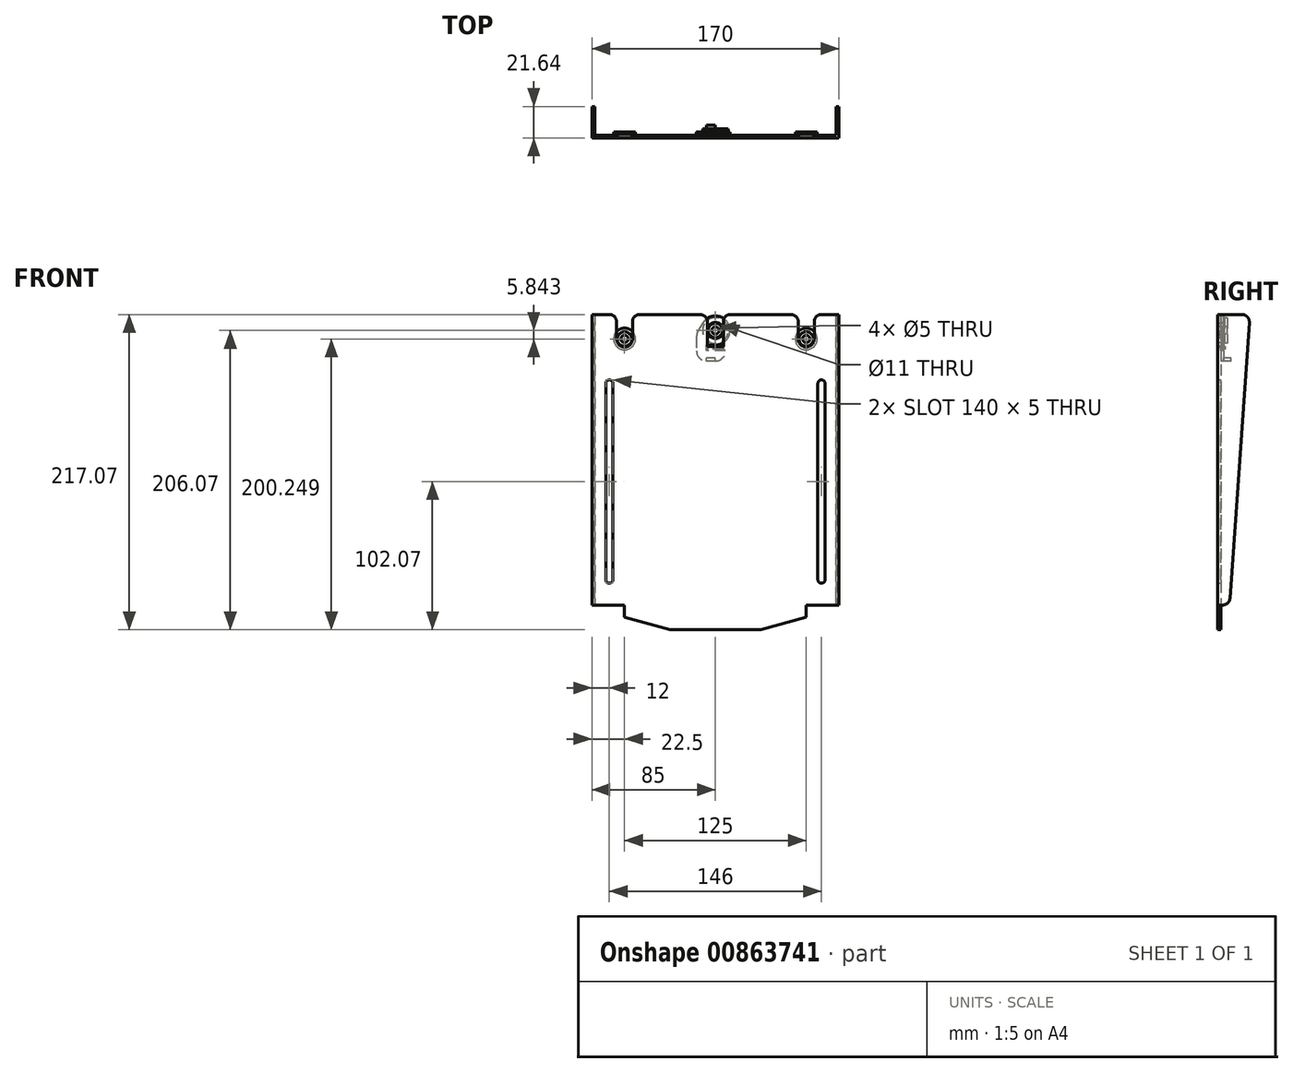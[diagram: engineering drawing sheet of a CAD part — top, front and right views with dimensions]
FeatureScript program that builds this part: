
annotation { "Feature Type Name" : "Feature", "Feature Type Description" : "" }
export const myFeature = defineFeature(function(context is Context, id is Id, definition is map)
    precondition{}
    {
        {
            var Q0;
            Q0=qCreatedBy(makeId("Front.planeOp"),FACE);
            var sketch = newSketch(context, id + "F0", { "sketchPlane" : qUnion([Q0])});
            skLineSegment(sketch, "E0.top", {"start": v(0, -100) * mm, "end": v(85, -100) * mm});
            skLineSegment(sketch, "E0.left", {"start": v(0, 100) * mm, "end": v(0, -100) * mm});
            skLineSegment(sketch, "E0.right", {"start": v(85, 100) * mm, "end": v(85, -100) * mm});
            skPoint(sketch, "E0.middle", {"position": v(42.5, 0) * mm});
            skLineSegment(sketch, "E1.left", {"start": v(0, 100) * mm, "end": v(0, 105) * mm});
            skLineSegment(sketch, "E2.MirrorCS", {"start": v(-85, 100) * mm, "end": v(-85, -100) * mm});
            skLineSegment(sketch, "E3.MirrorCS", {"start": v(0, -100) * mm, "end": v(-85, -100) * mm});
            skPoint(sketch, "E4.MirrorP", {"position": v(-42.5, 0) * mm});
            skLineSegment(sketch, "E5.bottom", {"start": v(73, -85) * mm, "end": v(73, -85) * mm});
            skLineSegment(sketch, "E5.top", {"start": v(73, 55) * mm, "end": v(73, 55) * mm});
            skLineSegment(sketch, "E5.left", {"start": v(70.5, -82.5) * mm, "end": v(70.5, 52.5) * mm});
            skLineSegment(sketch, "E5.right", {"start": v(75.5, -82.5) * mm, "end": v(75.5, 52.5) * mm});
            skPoint(sketch, "E5.middle", {"position": v(73, -15) * mm});
            skPoint(sketch, "E6.visualSharp", {"position": v(70.5, -85) * mm});
            skArc(sketch, "E6.filletArc", {"start": v(70.5, -82.5) * mm, "mid": v(71.23, -84.27) * mm, "end": v(73, -85) * mm});
            skPoint(sketch, "E7.visualSharp", {"position": v(75.5, -85) * mm});
            skArc(sketch, "E7.filletArc", {"start": v(73, -85) * mm, "mid": v(74.77, -84.27) * mm, "end": v(75.5, -82.5) * mm});
            skPoint(sketch, "E8.visualSharp", {"position": v(70.5, 55) * mm});
            skArc(sketch, "E8.filletArc", {"start": v(73, 55) * mm, "mid": v(71.23, 54.27) * mm, "end": v(70.5, 52.5) * mm});
            skPoint(sketch, "E9.visualSharp", {"position": v(75.5, 55) * mm});
            skArc(sketch, "E9.filletArc", {"start": v(75.5, 52.5) * mm, "mid": v(74.77, 54.27) * mm, "end": v(73, 55) * mm});
            skArc(sketch, "E10.MirrorCS", {"start": v(-70.5, -82.5) * mm, "mid": v(-71.23, -84.27) * mm, "end": v(-73, -85) * mm});
            skArc(sketch, "E11.MirrorCS", {"start": v(-75.5, 52.5) * mm, "mid": v(-74.77, 54.27) * mm, "end": v(-73, 55) * mm});
            skArc(sketch, "E12.MirrorCS", {"start": v(-73, -85) * mm, "mid": v(-74.77, -84.27) * mm, "end": v(-75.5, -82.5) * mm});
            skArc(sketch, "E13.MirrorCS", {"start": v(-73, 55) * mm, "mid": v(-71.23, 54.27) * mm, "end": v(-70.5, 52.5) * mm});
            skLineSegment(sketch, "E14.MirrorCS", {"start": v(-70.5, -82.5) * mm, "end": v(-70.5, 52.5) * mm});
            skLineSegment(sketch, "E15.MirrorCS", {"start": v(-75.5, -82.5) * mm, "end": v(-75.5, 52.5) * mm});
            skPoint(sketch, "E16.MirrorP", {"position": v(-70.5, -85) * mm});
            skPoint(sketch, "E17.MirrorP", {"position": v(-75.5, -85) * mm});
            skPoint(sketch, "E18.MirrorP", {"position": v(-75.5, 55) * mm});
            skPoint(sketch, "E19.MirrorP", {"position": v(-73, -15) * mm});
            skPoint(sketch, "E20.MirrorP", {"position": v(-70.5, 55) * mm});
            skLineSegment(sketch, "E21.MirrorCS", {"start": v(-73, -85) * mm, "end": v(-73, -85) * mm});
            skLineSegment(sketch, "E22.MirrorCS", {"start": v(-73, 55) * mm, "end": v(-73, 55) * mm});
            skLineSegment(sketch, "E23", {"start": v(0, -100) * mm, "end": v(0, -117.07) * mm});
            skLineSegment(sketch, "E24", {"start": v(0, -117.07) * mm, "end": v(-31.25, -117.07) * mm});
            skLineSegment(sketch, "E25", {"start": v(-62.5, -100) * mm, "end": v(-62.5, -108.5) * mm});
            skLineSegment(sketch, "E26", {"start": v(-62.5, -108.5) * mm, "end": v(-31.25, -117.07) * mm});
            skLineSegment(sketch, "E27.MirrorCS", {"start": v(62.5, -100) * mm, "end": v(62.5, -108.5) * mm});
            skLineSegment(sketch, "E28.MirrorCS", {"start": v(0, -117.07) * mm, "end": v(31.25, -117.07) * mm});
            skLineSegment(sketch, "E29.MirrorCS", {"start": v(62.5, -108.5) * mm, "end": v(31.25, -117.07) * mm});
            skLineSegment(sketch, "E30", {"start": v(-85, 100) * mm, "end": v(-73, 100) * mm});
            skLineSegment(sketch, "E31", {"start": v(-68, 95) * mm, "end": v(-68, 83.18) * mm});
            skLineSegment(sketch, "E32", {"start": v(-62.5, 77.68) * mm, "end": v(-62.5, 77.68) * mm});
            skLineSegment(sketch, "E33", {"start": v(-57, 83.18) * mm, "end": v(-57, 95) * mm});
            skPoint(sketch, "E34.visualSharp", {"position": v(-68, 77.68) * mm});
            skArc(sketch, "E34.filletArc", {"start": v(-68, 83.18) * mm, "mid": v(-66.39, 79.29) * mm, "end": v(-62.5, 77.68) * mm});
            skPoint(sketch, "E35.visualSharp", {"position": v(-57, 77.68) * mm});
            skArc(sketch, "E35.filletArc", {"start": v(-62.5, 77.68) * mm, "mid": v(-58.61, 79.29) * mm, "end": v(-57, 83.18) * mm});
            skLineSegment(sketch, "E36.MirrorCS", {"start": v(57, 83.18) * mm, "end": v(57, 95) * mm});
            skPoint(sketch, "E37.MirrorP", {"position": v(57, 77.68) * mm});
            skArc(sketch, "E38.MirrorCS", {"start": v(62.5, 77.68) * mm, "mid": v(58.61, 79.29) * mm, "end": v(57, 83.18) * mm});
            skArc(sketch, "E39.MirrorCS", {"start": v(68, 83.18) * mm, "mid": v(66.39, 79.29) * mm, "end": v(62.5, 77.68) * mm});
            skLineSegment(sketch, "E40.MirrorCS", {"start": v(68, 95) * mm, "end": v(68, 83.18) * mm});
            skLineSegment(sketch, "E41.MirrorCS", {"start": v(85, 100) * mm, "end": v(73, 100) * mm});
            skPoint(sketch, "E42.visualSharp", {"position": v(57, 100) * mm});
            skArc(sketch, "E42.filletArc", {"start": v(57, 95) * mm, "mid": v(55.54, 98.54) * mm, "end": v(52, 100) * mm});
            skPoint(sketch, "E43.visualSharp", {"position": v(68, 100) * mm});
            skArc(sketch, "E43.filletArc", {"start": v(73, 100) * mm, "mid": v(69.46, 98.54) * mm, "end": v(68, 95) * mm});
            skPoint(sketch, "E44.visualSharp", {"position": v(-57, 100) * mm});
            skArc(sketch, "E44.filletArc", {"start": v(-52, 100) * mm, "mid": v(-55.54, 98.54) * mm, "end": v(-57, 95) * mm});
            skPoint(sketch, "E45.visualSharp", {"position": v(-68, 100) * mm});
            skArc(sketch, "E45.filletArc", {"start": v(-68, 95) * mm, "mid": v(-69.46, 98.54) * mm, "end": v(-73, 100) * mm});
            skLineSegment(sketch, "E46", {"start": v(5.5, 95) * mm, "end": v(5.5, 78) * mm});
            skLineSegment(sketch, "E47", {"start": v(5.5, 78) * mm, "end": v(-5.5, 78) * mm});
            skLineSegment(sketch, "E48", {"start": v(-5.5, 78) * mm, "end": v(-5.5, 95) * mm});
            skLineSegment(sketch, "E49", {"start": v(52, 100) * mm, "end": v(10.5, 100) * mm});
            skLineSegment(sketch, "E50", {"start": v(-52, 100) * mm, "end": v(-10.5, 100) * mm});
            skPoint(sketch, "E51.visualSharp", {"position": v(-5.5, 100) * mm});
            skArc(sketch, "E51.filletArc", {"start": v(-5.5, 95) * mm, "mid": v(-6.96, 98.54) * mm, "end": v(-10.5, 100) * mm});
            skPoint(sketch, "E52.visualSharp", {"position": v(5.5, 100) * mm});
            skArc(sketch, "E52.filletArc", {"start": v(10.5, 100) * mm, "mid": v(6.96, 98.54) * mm, "end": v(5.5, 95) * mm});
            skSolve(sketch);
        }
        {
            var Q0;
            Q0=qSketchRegion(id+"F0",true);
            extrude(context, id + "F1", {"entities" : qUnion([Q0]), "depth" : 2 * mm, "offsetDistance" : 25 * mm});
        }
        {
            var Q0;
            Q0=makeQuery(id+"F1.opExtrude","CAP_FACE",FACE,{"disambiguationData":[OSD([sQuery(id+"F0.wireOp",EDGE,"E0.bottom"),sQuery(id+"F0.wireOp",EDGE,"E0.top"),sQuery(id+"F0.wireOp",EDGE,"E0.right"),sQuery(id+"F0.wireOp",EDGE,"frcyEhX3-ksV9-Io33-VOOh-hWverEK9uXBL.left"),sQuery(id+"F0.wireOp",EDGE,"frcyEhX3-ksV9-Io33-VOOh-hWverEK9uXBL.right"),sQuery(id+"F0.wireOp",EDGE,"ycnwuAfa-UpH9-AvOl-Gm3H-XGRiDgKgmbUQ"),sQuery(id+"F0.wireOp",EDGE,"YSR243FN-PfGp-wJLQ-lxfN-2wXKMQRAt0pg"),sQuery(id+"F0.wireOp",EDGE,"E1.bottom"),sQuery(id+"F0.wireOp",EDGE,"f4791902-98f6-4560-8930-070e0529dc460.MirrorCS"),sQuery(id+"F0.wireOp",EDGE,"f4791902-98f6-4560-8930-070e0529dc461.MirrorCS"),sQuery(id+"F0.wireOp",EDGE,"E2.MirrorCS"),sQuery(id+"F0.wireOp",EDGE,"f4791902-98f6-4560-8930-070e0529dc4612.MirrorCS"),sQuery(id+"F0.wireOp",EDGE,"f4791902-98f6-4560-8930-070e0529dc4615.MirrorCS"),sQuery(id+"F0.wireOp",EDGE,"E3.MirrorCS"),sQuery(id+"F0.wireOp",EDGE,"f4791902-98f6-4560-8930-070e0529dc4617.MirrorCS"),sQuery(id+"F0.wireOp",EDGE,"f4791902-98f6-4560-8930-070e0529dc4623.MirrorCS")])],"isStart":true});
            var sketch = newSketch(context, id + "F2", { "sketchPlane" : qUnion([Q0])});
            skArc(sketch, "E53", {"start": v(-10, 89) * mm, "mid": v(-7.07, 81.93) * mm, "end": v(0, 79) * mm});
            skCircle(sketch, "E54", {"center": v(0, 89) * mm, "radius": 5.5 * mm});
            skLineSegment(sketch, "E55", {"start": v(0, 79) * mm, "end": v(6, 79) * mm});
            skLineSegment(sketch, "E56", {"start": v(-7, 75) * mm, "end": v(6, 75) * mm});
            skLineSegment(sketch, "E57", {"start": v(6, 75) * mm, "end": v(6, 79) * mm});
            skArc(sketch, "E58", {"start": v(-7, 75) * mm, "mid": v(-4.95, 70.05) * mm, "end": v(0, 68) * mm});
            skLineSegment(sketch, "E59", {"start": v(13, 84.44) * mm, "end": v(13, 75) * mm});
            skLineSegment(sketch, "E60", {"start": v(0, 68) * mm, "end": v(6, 68) * mm});
            skPoint(sketch, "E61.visualSharp", {"position": v(13, 68) * mm});
            skArc(sketch, "E61.filletArc", {"start": v(6, 68) * mm, "mid": v(10.95, 70.05) * mm, "end": v(13, 75) * mm});
            skPoint(sketch, "E62.visualSharp", {"position": v(13, 89) * mm});
            skLineSegment(sketch, "E63", {"start": v(11.65, 89.18) * mm, "end": v(8.5, 94.26) * mm});
            skArc(sketch, "E64", {"start": v(0, 79) * mm, "mid": v(-8.74, 93.87) * mm, "end": v(8.5, 94.26) * mm});
            skPoint(sketch, "E65.visualSharp", {"position": v(13, 87) * mm});
            skArc(sketch, "E65.filletArc", {"start": v(13, 84.44) * mm, "mid": v(12.66, 86.9) * mm, "end": v(11.65, 89.18) * mm});
            skSolve(sketch);
        }
        {
            var Q0;
            Q0=qSketchRegion(id+"F2",true);
            extrude(context, id + "F3", {"entities" : qUnion([Q0]), "depth" : 2 * mm, "offsetDistance" : 25 * mm});
        }
        {
            var Q0;
            Q0=makeQuery(id+"F1.opExtrude","SWEPT_FACE",FACE,{"disambiguationData":[OSD([sQuery(id+"F0.wireOp",EDGE,"E2.MirrorCS")])]});
            var sketch = newSketch(context, id + "F4", { "sketchPlane" : qUnion([Q0])});
            skLineSegment(sketch, "E66", {"start": v(0, 100) * mm, "end": v(-14.64, 100) * mm});
            skLineSegment(sketch, "E67", {"start": v(0, -100) * mm, "end": v(-1.34, -100) * mm});
            skLineSegment(sketch, "E68", {"start": v(-6.33, -95.35) * mm, "end": v(-19.63, 94.65) * mm});
            skLineSegment(sketch, "E69", {"start": v(0, 100) * mm, "end": v(0, -100) * mm});
            skPoint(sketch, "E70.visualSharp", {"position": v(-20, 100) * mm});
            skArc(sketch, "E70.filletArc", {"start": v(-14.64, 100) * mm, "mid": v(-18.3, 98.4) * mm, "end": v(-19.63, 94.65) * mm});
            skPoint(sketch, "E71.visualSharp", {"position": v(-6, -100) * mm});
            skArc(sketch, "E71.filletArc", {"start": v(-6.33, -95.35) * mm, "mid": v(-4.75, -98.66) * mm, "end": v(-1.34, -100) * mm});
            skSolve(sketch);
        }
        {
            var Q0;
            Q0=qSketchRegion(id+"F4",true);
            extrude(context, id + "F5", {"entities" : qUnion([Q0]), "oppositeDirection" : true, "depth" : 2 * mm, "offsetDistance" : 25 * mm});
        }
        {
            var Q0;
            Q0=makeQuery(id+"F1.opExtrude","SWEPT_FACE",FACE,{"disambiguationData":[OSD([sQuery(id+"F0.wireOp",EDGE,"E0.right")])]});
            var sketch = newSketch(context, id + "F6", { "sketchPlane" : qUnion([Q0])});
            skLineSegment(sketch, "E72", {"start": v(0, 100) * mm, "end": v(14.64, 100) * mm});
            skLineSegment(sketch, "E73", {"start": v(0, -100) * mm, "end": v(1.34, -100) * mm});
            skLineSegment(sketch, "E74", {"start": v(6.33, -95.35) * mm, "end": v(19.63, 94.65) * mm});
            skLineSegment(sketch, "E75", {"start": v(0, 100) * mm, "end": v(0, -100) * mm});
            skPoint(sketch, "E76.visualSharp", {"position": v(6, -100) * mm});
            skArc(sketch, "E76.filletArc", {"start": v(1.34, -100) * mm, "mid": v(4.75, -98.66) * mm, "end": v(6.33, -95.35) * mm});
            skPoint(sketch, "E77.visualSharp", {"position": v(20, 100) * mm});
            skArc(sketch, "E77.filletArc", {"start": v(19.63, 94.65) * mm, "mid": v(18.3, 98.4) * mm, "end": v(14.64, 100) * mm});
            skSolve(sketch);
        }
        {
            var Q0;
            Q0=qSketchRegion(id+"F6",true);
            extrude(context, id + "F7", {"entities" : qUnion([Q0]), "operationType" : NewBodyOperationType.ADD, "oppositeDirection" : true, "depth" : 2 * mm, "offsetDistance" : 25 * mm});
        }
        {
            var Q0;
            Q0=qCreatedBy(makeId("Front.planeOp"),FACE);
            var sketch = newSketch(context, id + "F8", { "sketchPlane" : qUnion([Q0])});
            skLineSegment(sketch, "E78.bottom", {"start": v(5.5, 78) * mm, "end": v(-5.46, 78) * mm});
            skLineSegment(sketch, "E78.top", {"start": v(5.5, 76.07) * mm, "end": v(-5.46, 76.07) * mm});
            skLineSegment(sketch, "E78.left", {"start": v(5.5, 78) * mm, "end": v(5.5, 76.07) * mm});
            skLineSegment(sketch, "E78.right", {"start": v(-5.46, 78) * mm, "end": v(-5.46, 76.07) * mm});
            skSolve(sketch);
        }
        {
            var Q0;
            Q0=qSketchRegion(id+"F8",true);
            extrude(context, id + "F9", {"entities" : qUnion([Q0]), "operationType" : NewBodyOperationType.ADD, "oppositeDirection" : true, "depth" : 3 * mm, "offsetDistance" : 25 * mm});
        }
        {
            var Q0;
            Q0=makeQuery(id+"F1.opExtrude","CAP_FACE",FACE,{"disambiguationData":[OSD([sQuery(id+"F0.wireOp",EDGE,"E0.right"),sQuery(id+"F0.wireOp",EDGE,"E2.MirrorCS"),sQuery(id+"F0.wireOp",EDGE,"E5.left"),sQuery(id+"F0.wireOp",EDGE,"E5.right"),sQuery(id+"F0.wireOp",EDGE,"E6.filletArc"),sQuery(id+"F0.wireOp",EDGE,"E7.filletArc"),sQuery(id+"F0.wireOp",EDGE,"E8.filletArc"),sQuery(id+"F0.wireOp",EDGE,"E9.filletArc"),sQuery(id+"F0.wireOp",EDGE,"E10.MirrorCS"),sQuery(id+"F0.wireOp",EDGE,"E13.MirrorCS"),sQuery(id+"F0.wireOp",EDGE,"E12.MirrorCS"),sQuery(id+"F0.wireOp",EDGE,"E11.MirrorCS"),sQuery(id+"F0.wireOp",EDGE,"E14.MirrorCS"),sQuery(id+"F0.wireOp",EDGE,"E15.MirrorCS"),sQuery(id+"F0.wireOp",EDGE,"E24"),sQuery(id+"F0.wireOp",EDGE,"E25"),sQuery(id+"F0.wireOp",EDGE,"E26"),sQuery(id+"F0.wireOp",EDGE,"E27.MirrorCS"),sQuery(id+"F0.wireOp",EDGE,"E28.MirrorCS"),sQuery(id+"F0.wireOp",EDGE,"E29.MirrorCS"),sQuery(id+"F0.wireOp",EDGE,"E3.MirrorCS"),sQuery(id+"F0.wireOp",EDGE,"E0.top"),sQuery(id+"F0.wireOp",EDGE,"E30"),sQuery(id+"F0.wireOp",EDGE,"E31"),sQuery(id+"F0.wireOp",EDGE,"E33"),sQuery(id+"F0.wireOp",EDGE,"E34.filletArc"),sQuery(id+"F0.wireOp",EDGE,"E35.filletArc"),sQuery(id+"F0.wireOp",EDGE,"E36.MirrorCS"),sQuery(id+"F0.wireOp",EDGE,"E38.MirrorCS"),sQuery(id+"F0.wireOp",EDGE,"E39.MirrorCS"),sQuery(id+"F0.wireOp",EDGE,"E40.MirrorCS"),sQuery(id+"F0.wireOp",EDGE,"E41.MirrorCS"),sQuery(id+"F0.wireOp",EDGE,"E42.filletArc"),sQuery(id+"F0.wireOp",EDGE,"E43.filletArc"),sQuery(id+"F0.wireOp",EDGE,"E44.filletArc"),sQuery(id+"F0.wireOp",EDGE,"E45.filletArc"),sQuery(id+"F0.wireOp",EDGE,"E46"),sQuery(id+"F0.wireOp",EDGE,"E47"),sQuery(id+"F0.wireOp",EDGE,"E48"),sQuery(id+"F0.wireOp",EDGE,"E49"),sQuery(id+"F0.wireOp",EDGE,"E50"),sQuery(id+"F0.wireOp",EDGE,"E51.filletArc"),sQuery(id+"F0.wireOp",EDGE,"E52.filletArc")])],"isStart":false});
            var sketch = newSketch(context, id + "F10", { "sketchPlane" : qUnion([Q0])});
            skCircle(sketch, "E79", {"center": v(0, 89.02) * mm, "radius": 5 * mm});
            skCircle(sketch, "E80", {"center": v(0, 89.02) * mm, "radius": 2.5 * mm});
            skSolve(sketch);
        }
        {
            var Q0;
            Q0=qSketchRegion(id+"F10",true);
            extrude(context, id + "F11", {"entities" : qUnion([Q0]), "oppositeDirection" : true, "depth" : 4.5 * mm, "offsetDistance" : 25 * mm});
        }
        {
            var Q0;
            Q0=makeQuery(id+"F11.opExtrude","CAP_FACE",FACE,{"disambiguationData":[OSD([sQuery(id+"F10.wireOp",EDGE,"E79"),sQuery(id+"F10.wireOp",EDGE,"E80")])],"isStart":false});
            var sketch = newSketch(context, id + "F12", { "sketchPlane" : qUnion([Q0])});
            skCircle(sketch, "E81", {"center": v(0, 89.02) * mm, "radius": 2.5 * mm});
            skCircle(sketch, "E82", {"center": v(0, 89.02) * mm, "radius": 8.84 * mm});
            skSolve(sketch);
        }
        {
            var Q0;
            Q0=qSketchRegion(id+"F12",true);
            extrude(context, id + "F13", {"entities" : qUnion([Q0]), "depth" : 2 * mm, "offsetDistance" : 25 * mm});
        }
        {
            var Q0;
            Q0=makeQuery(id+"F3.opExtrude","CAP_FACE",FACE,{"disambiguationData":[OSD([sQuery(id+"F2.wireOp",EDGE,"E54"),sQuery(id+"F2.wireOp",EDGE,"E55"),sQuery(id+"F2.wireOp",EDGE,"E56"),sQuery(id+"F2.wireOp",EDGE,"E57"),sQuery(id+"F2.wireOp",EDGE,"E58"),sQuery(id+"F2.wireOp",EDGE,"E59"),sQuery(id+"F2.wireOp",EDGE,"E60"),sQuery(id+"F2.wireOp",EDGE,"E61.filletArc"),sQuery(id+"F2.wireOp",EDGE,"E63"),sQuery(id+"F2.wireOp",EDGE,"E64"),sQuery(id+"F2.wireOp",EDGE,"E65.filletArc")])],"isStart":false});
            var sketch = newSketch(context, id + "F14", { "sketchPlane" : qUnion([Q0])});
            skLineSegment(sketch, "E83.bottom", {"start": v(0, 68) * mm, "end": v(6, 68) * mm});
            skLineSegment(sketch, "E83.top", {"start": v(0, 70) * mm, "end": v(6, 70) * mm});
            skLineSegment(sketch, "E83.left", {"start": v(0, 68) * mm, "end": v(0, 70) * mm});
            skLineSegment(sketch, "E83.right", {"start": v(6, 68) * mm, "end": v(6, 70) * mm});
            skSolve(sketch);
        }
        {
            var Q0;
            Q0=qSketchRegion(id+"F14",true);
            extrude(context, id + "F15", {"entities" : qUnion([Q0]), "operationType" : NewBodyOperationType.ADD, "depth" : 5 * mm, "offsetDistance" : 25 * mm});
        }
        {
            var Q0;
            Q0=makeQuery(id+"F1.opExtrude","CAP_FACE",FACE,{"disambiguationData":[OSD([sQuery(id+"F0.wireOp",EDGE,"E0.right"),sQuery(id+"F0.wireOp",EDGE,"E2.MirrorCS"),sQuery(id+"F0.wireOp",EDGE,"E5.left"),sQuery(id+"F0.wireOp",EDGE,"E5.right"),sQuery(id+"F0.wireOp",EDGE,"E6.filletArc"),sQuery(id+"F0.wireOp",EDGE,"E7.filletArc"),sQuery(id+"F0.wireOp",EDGE,"E8.filletArc"),sQuery(id+"F0.wireOp",EDGE,"E9.filletArc"),sQuery(id+"F0.wireOp",EDGE,"E10.MirrorCS"),sQuery(id+"F0.wireOp",EDGE,"E13.MirrorCS"),sQuery(id+"F0.wireOp",EDGE,"E12.MirrorCS"),sQuery(id+"F0.wireOp",EDGE,"E11.MirrorCS"),sQuery(id+"F0.wireOp",EDGE,"E14.MirrorCS"),sQuery(id+"F0.wireOp",EDGE,"E15.MirrorCS"),sQuery(id+"F0.wireOp",EDGE,"E24"),sQuery(id+"F0.wireOp",EDGE,"E25"),sQuery(id+"F0.wireOp",EDGE,"E26"),sQuery(id+"F0.wireOp",EDGE,"E27.MirrorCS"),sQuery(id+"F0.wireOp",EDGE,"E28.MirrorCS"),sQuery(id+"F0.wireOp",EDGE,"E29.MirrorCS"),sQuery(id+"F0.wireOp",EDGE,"E3.MirrorCS"),sQuery(id+"F0.wireOp",EDGE,"E0.top"),sQuery(id+"F0.wireOp",EDGE,"E30"),sQuery(id+"F0.wireOp",EDGE,"E31"),sQuery(id+"F0.wireOp",EDGE,"E33"),sQuery(id+"F0.wireOp",EDGE,"E34.filletArc"),sQuery(id+"F0.wireOp",EDGE,"E35.filletArc"),sQuery(id+"F0.wireOp",EDGE,"E36.MirrorCS"),sQuery(id+"F0.wireOp",EDGE,"E38.MirrorCS"),sQuery(id+"F0.wireOp",EDGE,"E39.MirrorCS"),sQuery(id+"F0.wireOp",EDGE,"E40.MirrorCS"),sQuery(id+"F0.wireOp",EDGE,"E41.MirrorCS"),sQuery(id+"F0.wireOp",EDGE,"E42.filletArc"),sQuery(id+"F0.wireOp",EDGE,"E43.filletArc"),sQuery(id+"F0.wireOp",EDGE,"E44.filletArc"),sQuery(id+"F0.wireOp",EDGE,"E45.filletArc"),sQuery(id+"F0.wireOp",EDGE,"E46"),sQuery(id+"F0.wireOp",EDGE,"E47"),sQuery(id+"F0.wireOp",EDGE,"E48"),sQuery(id+"F0.wireOp",EDGE,"E49"),sQuery(id+"F0.wireOp",EDGE,"E50"),sQuery(id+"F0.wireOp",EDGE,"E51.filletArc"),sQuery(id+"F0.wireOp",EDGE,"E52.filletArc")])],"isStart":false});
            var sketch = newSketch(context, id + "F16", { "sketchPlane" : qUnion([Q0])});
            skCircle(sketch, "E84", {"center": v(-62.5, 83.18) * mm, "radius": 5 * mm});
            skCircle(sketch, "E85", {"center": v(-62.5, 83.18) * mm, "radius": 2.5 * mm});
            skSolve(sketch);
        }
        {
            var Q0;
            Q0=qSketchRegion(id+"F16",true);
            extrude(context, id + "F17", {"entities" : qUnion([Q0]), "oppositeDirection" : true, "depth" : 3 * mm, "offsetDistance" : 25 * mm});
        }
        {
            var Q0;
            Q0=makeQuery(id+"F17.opExtrude","CAP_FACE",FACE,{"disambiguationData":[OSD([sQuery(id+"F16.wireOp",EDGE,"E84"),sQuery(id+"F16.wireOp",EDGE,"E85")])],"isStart":false});
            var sketch = newSketch(context, id + "F18", { "sketchPlane" : qUnion([Q0])});
            skCircle(sketch, "E86", {"center": v(62.5, 83.18) * mm, "radius": 7.5 * mm});
            skCircle(sketch, "E87", {"center": v(62.5, 83.18) * mm, "radius": 2.5 * mm});
            skSolve(sketch);
        }
        {
            var Q0;
            Q0=qSketchRegion(id+"F18",true);
            extrude(context, id + "F19", {"entities" : qUnion([Q0]), "operationType" : NewBodyOperationType.ADD, "depth" : 1 * mm, "offsetDistance" : 25 * mm});
        }
        {
            var Q0;
            Q0=makeQuery(id+"F1.opExtrude","CAP_FACE",FACE,{"disambiguationData":[OSD([sQuery(id+"F0.wireOp",EDGE,"E0.right"),sQuery(id+"F0.wireOp",EDGE,"E2.MirrorCS"),sQuery(id+"F0.wireOp",EDGE,"E5.left"),sQuery(id+"F0.wireOp",EDGE,"E5.right"),sQuery(id+"F0.wireOp",EDGE,"E6.filletArc"),sQuery(id+"F0.wireOp",EDGE,"E7.filletArc"),sQuery(id+"F0.wireOp",EDGE,"E8.filletArc"),sQuery(id+"F0.wireOp",EDGE,"E9.filletArc"),sQuery(id+"F0.wireOp",EDGE,"E10.MirrorCS"),sQuery(id+"F0.wireOp",EDGE,"E13.MirrorCS"),sQuery(id+"F0.wireOp",EDGE,"E12.MirrorCS"),sQuery(id+"F0.wireOp",EDGE,"E11.MirrorCS"),sQuery(id+"F0.wireOp",EDGE,"E14.MirrorCS"),sQuery(id+"F0.wireOp",EDGE,"E15.MirrorCS"),sQuery(id+"F0.wireOp",EDGE,"E24"),sQuery(id+"F0.wireOp",EDGE,"E25"),sQuery(id+"F0.wireOp",EDGE,"E26"),sQuery(id+"F0.wireOp",EDGE,"E27.MirrorCS"),sQuery(id+"F0.wireOp",EDGE,"E28.MirrorCS"),sQuery(id+"F0.wireOp",EDGE,"E29.MirrorCS"),sQuery(id+"F0.wireOp",EDGE,"E3.MirrorCS"),sQuery(id+"F0.wireOp",EDGE,"E0.top"),sQuery(id+"F0.wireOp",EDGE,"E30"),sQuery(id+"F0.wireOp",EDGE,"E31"),sQuery(id+"F0.wireOp",EDGE,"E33"),sQuery(id+"F0.wireOp",EDGE,"E34.filletArc"),sQuery(id+"F0.wireOp",EDGE,"E35.filletArc"),sQuery(id+"F0.wireOp",EDGE,"E36.MirrorCS"),sQuery(id+"F0.wireOp",EDGE,"E38.MirrorCS"),sQuery(id+"F0.wireOp",EDGE,"E39.MirrorCS"),sQuery(id+"F0.wireOp",EDGE,"E40.MirrorCS"),sQuery(id+"F0.wireOp",EDGE,"E41.MirrorCS"),sQuery(id+"F0.wireOp",EDGE,"E42.filletArc"),sQuery(id+"F0.wireOp",EDGE,"E43.filletArc"),sQuery(id+"F0.wireOp",EDGE,"E44.filletArc"),sQuery(id+"F0.wireOp",EDGE,"E45.filletArc"),sQuery(id+"F0.wireOp",EDGE,"E46"),sQuery(id+"F0.wireOp",EDGE,"E47"),sQuery(id+"F0.wireOp",EDGE,"E48"),sQuery(id+"F0.wireOp",EDGE,"E49"),sQuery(id+"F0.wireOp",EDGE,"E50"),sQuery(id+"F0.wireOp",EDGE,"E51.filletArc"),sQuery(id+"F0.wireOp",EDGE,"E52.filletArc")])],"isStart":false});
            var sketch = newSketch(context, id + "F20", { "sketchPlane" : qUnion([Q0])});
            skCircle(sketch, "E88", {"center": v(62.5, 83.18) * mm, "radius": 5 * mm});
            skCircle(sketch, "E89", {"center": v(62.5, 83.18) * mm, "radius": 2.5 * mm});
            skSolve(sketch);
        }
        {
            var Q0;
            Q0=qSketchRegion(id+"F20",true);
            extrude(context, id + "F21", {"entities" : qUnion([Q0]), "oppositeDirection" : true, "depth" : 3 * mm, "offsetDistance" : 25 * mm});
        }
        {
            var Q0;
            Q0=makeQuery(id+"F21.opExtrude","CAP_FACE",FACE,{"disambiguationData":[OSD([sQuery(id+"F20.wireOp",EDGE,"E88"),sQuery(id+"F20.wireOp",EDGE,"E89")])],"isStart":false});
            var sketch = newSketch(context, id + "F22", { "sketchPlane" : qUnion([Q0])});
            skCircle(sketch, "E90", {"center": v(-62.5, 83.18) * mm, "radius": 7.5 * mm});
            skCircle(sketch, "E91", {"center": v(-62.5, 83.18) * mm, "radius": 2.5 * mm});
            skSolve(sketch);
        }
        {
            var Q0;
            Q0=qSketchRegion(id+"F22",true);
            extrude(context, id + "F23", {"entities" : qUnion([Q0]), "operationType" : NewBodyOperationType.ADD, "depth" : 1 * mm, "offsetDistance" : 25 * mm});
        }
    });
